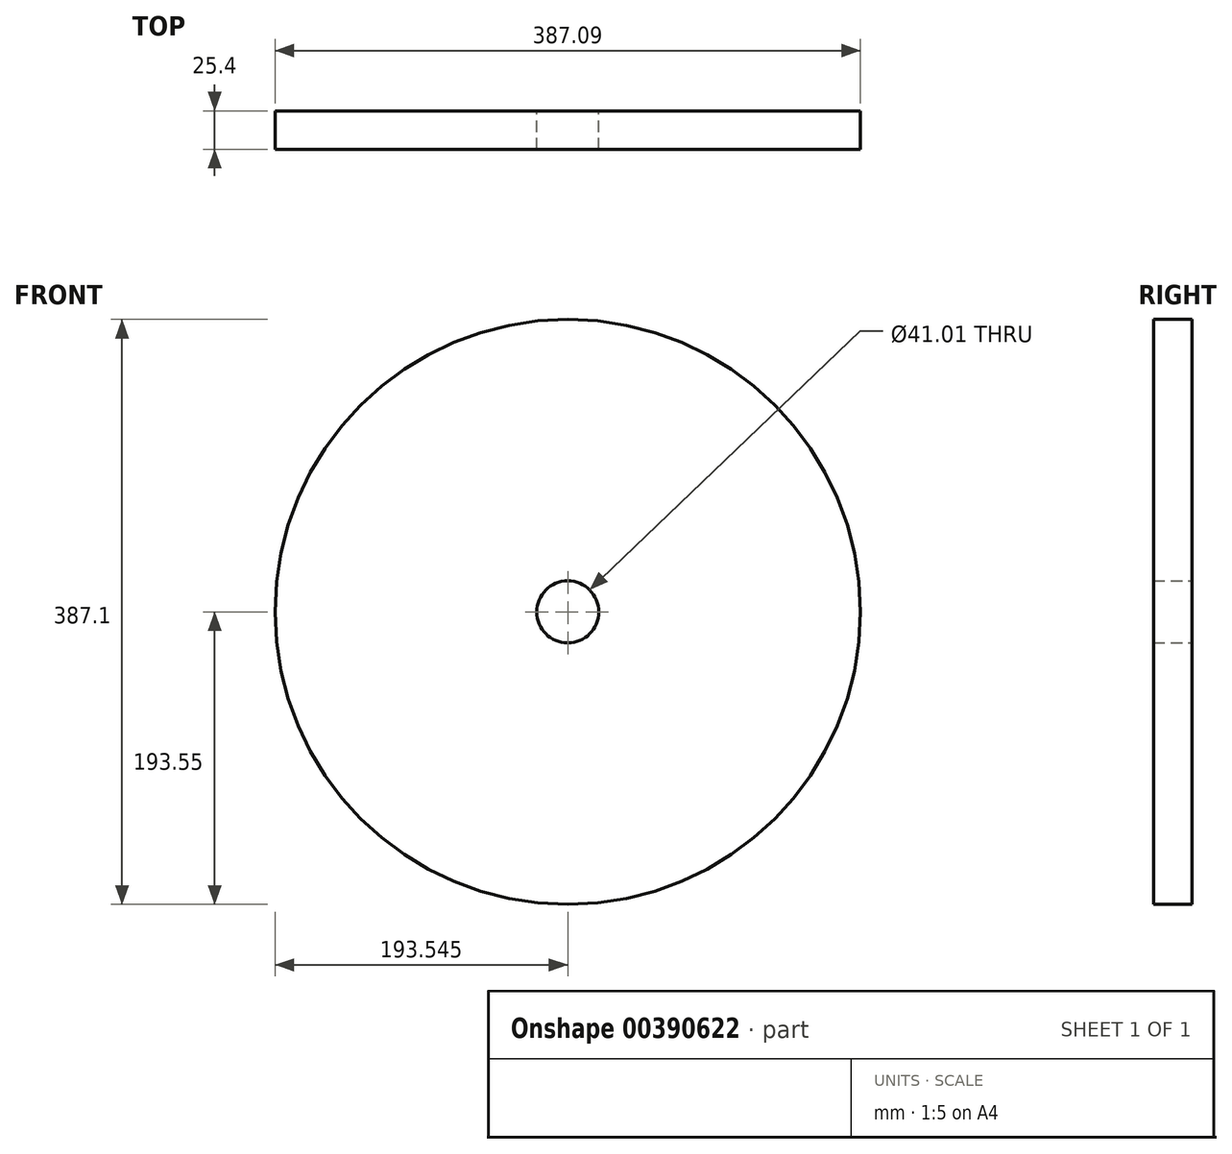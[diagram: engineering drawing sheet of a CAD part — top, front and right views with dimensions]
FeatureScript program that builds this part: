
annotation { "Feature Type Name" : "Feature", "Feature Type Description" : "" }
export const myFeature = defineFeature(function(context is Context, id is Id, definition is map)
    precondition{}
    {
        {
            var Q0;
            Q0=qCreatedBy(makeId("Front.planeOp"),FACE);
            var sketch = newSketch(context, id + "F0", { "sketchPlane" : qUnion([Q0])});
            skCircle(sketch, "E0", {"center": v(-20.65, 9.28) * mm, "radius": 5.63 * mm});
            skCircle(sketch, "E1", {"center": v(-20.65, 9.28) * mm, "radius": 193.55 * mm});
            skCircle(sketch, "E2", {"center": v(-20.65, 9.28) * mm, "radius": 20.5 * mm});
            skSolve(sketch);
        }
        {
            var Q0;
            Q0=makeQuery(id+"F0.imprint","IMPRINT",FACE,{"disambiguationData":[TD([[makeQuery(id+"F0.imprint","IMPRINT",EDGE,{"derivedFrom":sQuery(id+"F0.wireOp",EDGE,"E1")}),1.0]])]});
            extrude(context, id + "F1", {"entities" : qUnion([Q0]), "depth" : 25.4 * mm});
        }
    });
